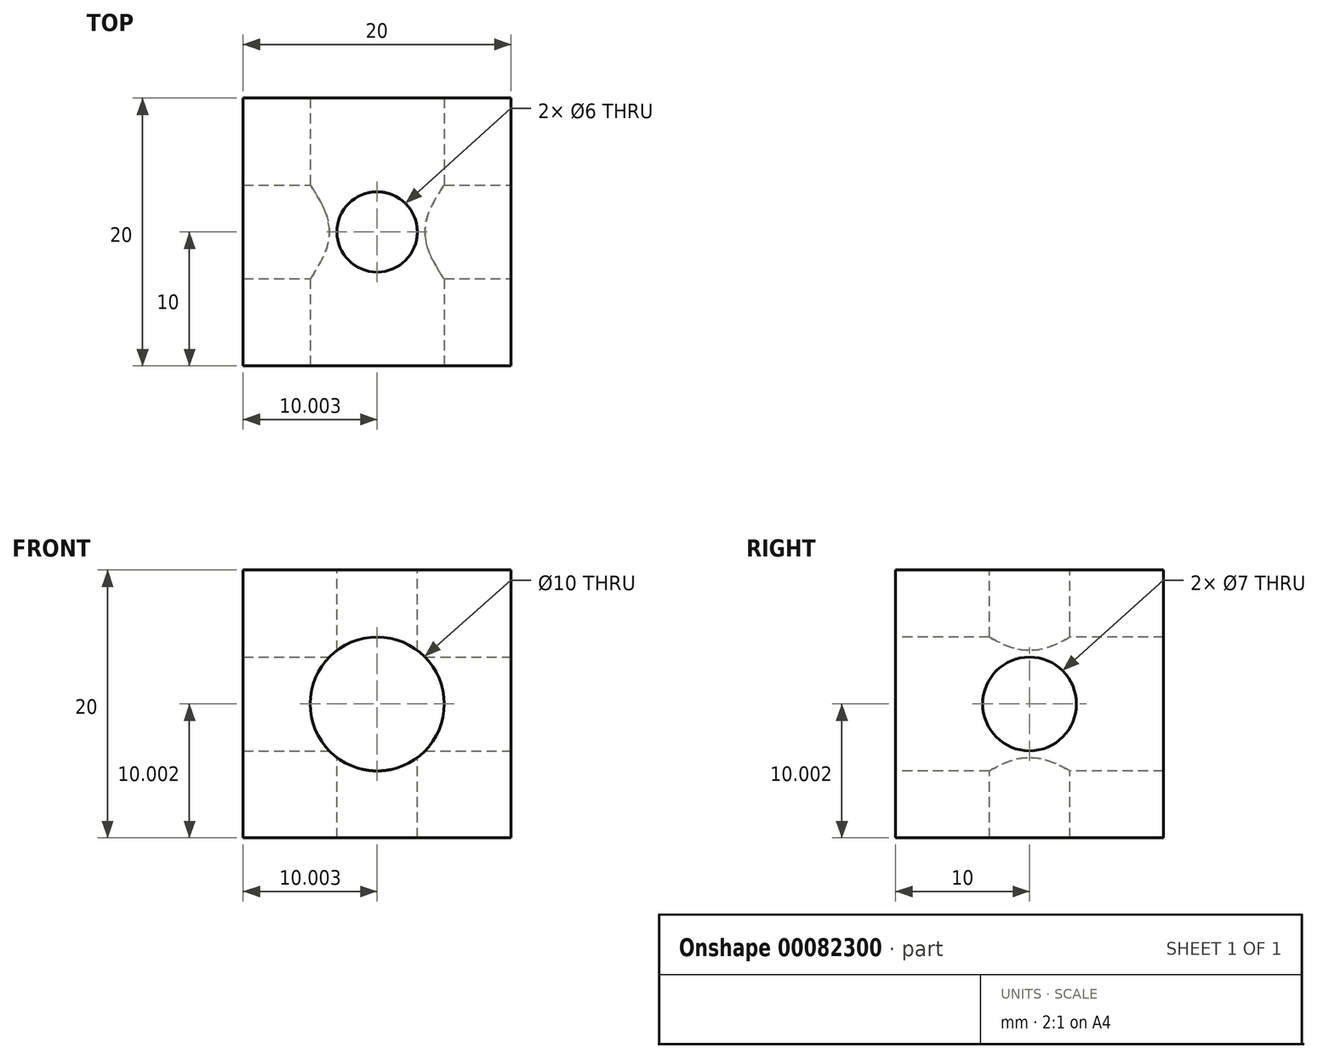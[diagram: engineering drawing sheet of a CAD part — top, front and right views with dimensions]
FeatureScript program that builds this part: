
annotation { "Feature Type Name" : "Feature", "Feature Type Description" : "" }
export const myFeature = defineFeature(function(context is Context, id is Id, definition is map)
    precondition{}
    {
        {
            var Q0;
            Q0=qCreatedBy(makeId("Front.planeOp"),FACE);
            var sketch = newSketch(context, id + "F0", { "sketchPlane" : qUnion([Q0])});
            skLineSegment(sketch, "E0.bottom", {"start": v(5.51, 3.1) * mm, "end": v(25.51, 3.1) * mm});
            skLineSegment(sketch, "E0.top", {"start": v(5.51, -16.9) * mm, "end": v(25.51, -16.9) * mm});
            skLineSegment(sketch, "E0.left", {"start": v(5.51, 3.1) * mm, "end": v(5.51, -16.9) * mm});
            skLineSegment(sketch, "E0.right", {"start": v(25.51, 3.1) * mm, "end": v(25.51, -16.9) * mm});
            skSolve(sketch);
        }
        {
            var Q0;
            Q0=makeQuery(id+"F0.imprint","IMPRINT",FACE,{"disambiguationData":[TD([[makeQuery(id+"F0.imprint","IMPRINT",EDGE,{"derivedFrom":sQuery(id+"F0.wireOp",EDGE,"E0.bottom")}),-1.0]])]});
            extrude(context, id + "F1", {"entities" : qUnion([Q0]), "depth" : 20 * mm});
        }
        {
            var Q0;
            Q0=makeQuery(id+"F1.opExtrude","SWEPT_FACE",FACE,{"disambiguationData":[OSD([sQuery(id+"F0.wireOp",EDGE,"E0.bottom")])]});
            var sketch = newSketch(context, id + "F2", { "sketchPlane" : qUnion([Q0])});
            skCircle(sketch, "E1", {"center": v(15.51, -10) * mm, "radius": 3 * mm});
            skSolve(sketch);
        }
        {
            var Q0;
            Q0=makeQuery(id+"F2.imprint","IMPRINT",FACE,{"disambiguationData":[TD([[makeQuery(id+"F2.imprint","IMPRINT",EDGE,{"derivedFrom":sQuery(id+"F2.wireOp",EDGE,"E1")}),1.0]])]});
            extrude(context, id + "F3", {"entities" : qUnion([Q0]), "operationType" : NewBodyOperationType.REMOVE, "oppositeDirection" : true, "depth" : 25 * mm});
        }
        {
            var Q0;
            Q0=makeQuery(id+"F1.opExtrude","SWEPT_FACE",FACE,{"disambiguationData":[OSD([sQuery(id+"F0.wireOp",EDGE,"E0.right")])]});
            var sketch = newSketch(context, id + "F4", { "sketchPlane" : qUnion([Q0])});
            skCircle(sketch, "E2", {"center": v(-10, -6.9) * mm, "radius": 3.5 * mm});
            skSolve(sketch);
        }
        {
            var Q0;
            Q0=makeQuery(id+"F4.imprint","IMPRINT",FACE,{"disambiguationData":[TD([[makeQuery(id+"F4.imprint","IMPRINT",EDGE,{"derivedFrom":sQuery(id+"F4.wireOp",EDGE,"E2")}),1.0]])]});
            extrude(context, id + "F5", {"entities" : qUnion([Q0]), "operationType" : NewBodyOperationType.REMOVE, "oppositeDirection" : true, "depth" : 25 * mm});
        }
        {
            var Q0;
            Q0=makeQuery(id+"F1.opExtrude","CAP_FACE",FACE,{"disambiguationData":[OSD([sQuery(id+"F0.wireOp",EDGE,"E0.bottom"),sQuery(id+"F0.wireOp",EDGE,"E0.top"),sQuery(id+"F0.wireOp",EDGE,"E0.left"),sQuery(id+"F0.wireOp",EDGE,"E0.right")])],"isStart":false});
            var sketch = newSketch(context, id + "F6", { "sketchPlane" : qUnion([Q0])});
            skCircle(sketch, "E3", {"center": v(15.51, -6.9) * mm, "radius": 5 * mm});
            skSolve(sketch);
        }
        {
            var Q0;
            Q0=makeQuery(id+"F6.imprint","IMPRINT",FACE,{"disambiguationData":[TD([[makeQuery(id+"F6.imprint","IMPRINT",EDGE,{"derivedFrom":sQuery(id+"F6.wireOp",EDGE,"E3")}),1.0]])]});
            extrude(context, id + "F7", {"entities" : qUnion([Q0]), "operationType" : NewBodyOperationType.REMOVE, "oppositeDirection" : true, "depth" : 25 * mm});
        }
    });
